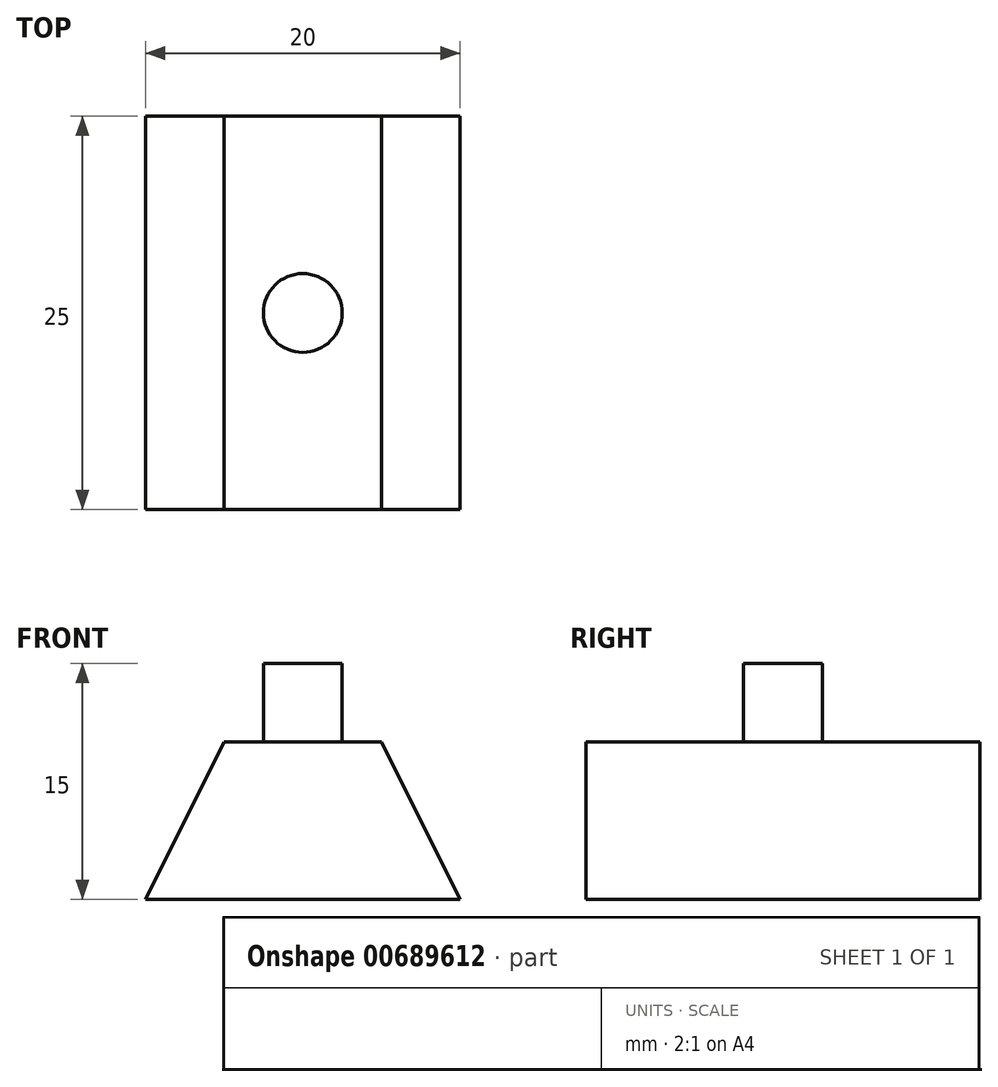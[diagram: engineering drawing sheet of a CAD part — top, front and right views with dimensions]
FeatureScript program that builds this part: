
annotation { "Feature Type Name" : "Feature", "Feature Type Description" : "" }
export const myFeature = defineFeature(function(context is Context, id is Id, definition is map)
    precondition{}
    {
        {
            var Q0;
            Q0=qCreatedBy(makeId("Front.planeOp"),FACE);
            var sketch = newSketch(context, id + "F0", { "sketchPlane" : qUnion([Q0])});
            skLineSegment(sketch, "E0", {"start": v(0, 26) * mm, "end": v(0, -10) * mm, "construction": true});
            skLineSegment(sketch, "E1", {"start": v(0, 0) * mm, "end": v(10, 0) * mm});
            skLineSegment(sketch, "E2.MirrorCS", {"start": v(0, -26) * mm, "end": v(0, 10) * mm, "construction": true});
            skLineSegment(sketch, "E3", {"start": v(0, 0) * mm, "end": v(-10, 0) * mm});
            skLineSegment(sketch, "E4", {"start": v(0, 10) * mm, "end": v(5, 10) * mm});
            skLineSegment(sketch, "E5", {"start": v(0, 10) * mm, "end": v(-5, 10) * mm});
            skLineSegment(sketch, "E6", {"start": v(-10, 0) * mm, "end": v(-5, 10) * mm});
            skLineSegment(sketch, "E7", {"start": v(5, 10) * mm, "end": v(10, 0) * mm});
            skSolve(sketch);
        }
        {
            var Q0;
            Q0=makeQuery(id+"F0.imprint","IMPRINT",FACE,{"disambiguationData":[TD([[makeQuery(id+"F0.imprint","IMPRINT",EDGE,{"derivedFrom":sQuery(id+"F0.wireOp",EDGE,"E1")}),1.0]])]});
            extrude(context, id + "F1", {"entities" : qUnion([Q0]), "depth" : 25 * mm, "offsetDistance" : 25 * mm});
        }
        {
            var Q0;
            Q0=makeQuery(id+"F1.opExtrude","SWEPT_FACE",FACE,{"disambiguationData":[OSD([sQuery(id+"F0.wireOp",EDGE,"E4"),sQuery(id+"F0.wireOp",EDGE,"E5")])]});
            var sketch = newSketch(context, id + "F2", { "sketchPlane" : qUnion([Q0])});
            skCircle(sketch, "E8", {"center": v(0, -12.5) * mm, "radius": 2.5 * mm});
            skPoint(sketch, "E8.centerSnap0", {"position": v(0, -25) * mm});
            skSolve(sketch);
        }
        {
            var Q0;
            Q0=makeQuery(id+"F2.imprint","IMPRINT",FACE,{"disambiguationData":[TD([[makeQuery(id+"F2.imprint","IMPRINT",EDGE,{"derivedFrom":sQuery(id+"F2.wireOp",EDGE,"E8")}),1.0]])]});
            extrude(context, id + "F3", {"entities" : qUnion([Q0]), "operationType" : NewBodyOperationType.ADD, "depth" : 5 * mm, "offsetDistance" : 25 * mm});
        }
    });
